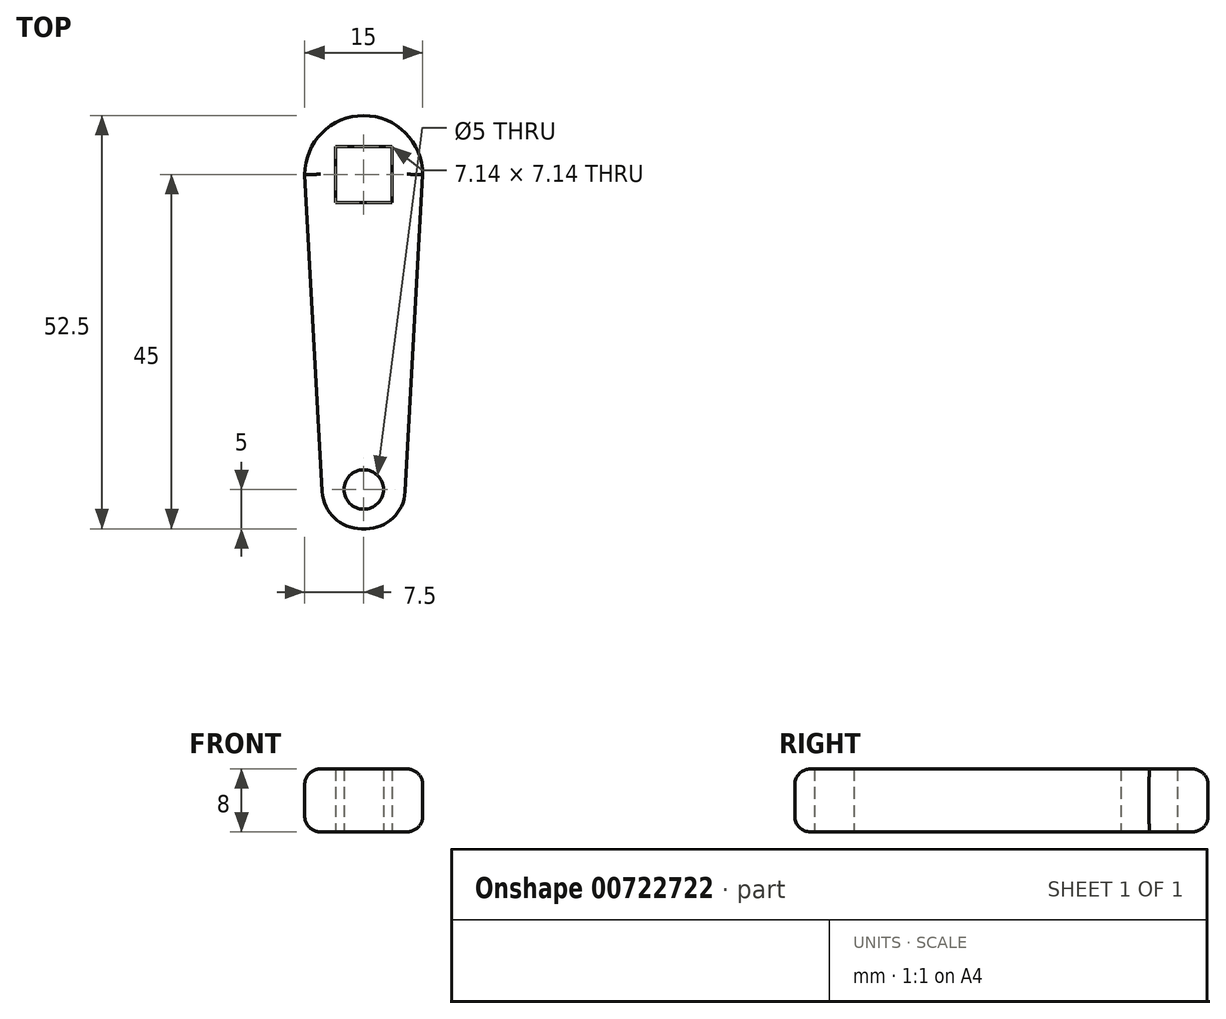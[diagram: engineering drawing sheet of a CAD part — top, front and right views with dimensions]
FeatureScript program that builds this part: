
annotation { "Feature Type Name" : "Feature", "Feature Type Description" : "" }
export const myFeature = defineFeature(function(context is Context, id is Id, definition is map)
    precondition{}
    {
        {
            var Q0;
            Q0=qCreatedBy(makeId("Top.planeOp"),FACE);
            var sketch = newSketch(context, id + "F0", { "sketchPlane" : qUnion([Q0])});
            skCircle(sketch, "E0.cCircle", {"center": v(0, 0) * mm, "radius": 5.05 * mm, "construction": true});
            skArc(sketch, "E1", {"start": v(7.5, 0) * mm, "mid": v(0, 7.5) * mm, "end": v(-7.5, 0) * mm});
            skLineSegment(sketch, "E2", {"start": v(0, 0) * mm, "end": v(0, -45) * mm, "construction": true});
            skLineSegment(sketch, "E3.bottom", {"start": v(-7.5, 0) * mm, "end": v(7.5, 0) * mm});
            skLineSegment(sketch, "E4", {"start": v(0, -45) * mm, "end": v(5, -45) * mm});
            skLineSegment(sketch, "E5", {"start": v(0, -45) * mm, "end": v(-5, -45) * mm});
            skLineSegment(sketch, "E6", {"start": v(-7.5, 0) * mm, "end": v(-5, -45) * mm});
            skLineSegment(sketch, "E7", {"start": v(7.5, 0) * mm, "end": v(5, -45) * mm});
            skLineSegment(sketch, "E8", {"start": v(0, -45) * mm, "end": v(0, -40) * mm, "construction": true});
            skCircle(sketch, "E9", {"center": v(0, -40) * mm, "radius": 2.5 * mm});
            skPoint(sketch, "E10.orphan", {"position": v(2.97, 4.09) * mm});
            skPoint(sketch, "E0.4.end.orphan", {"position": v(0, -5.05) * mm});
            skPoint(sketch, "E11.orphan", {"position": v(-4.8, -1.56) * mm});
            skLineSegment(sketch, "E12.0", {"start": v(3.57, -3.57) * mm, "end": v(-3.57, -3.57) * mm});
            skLineSegment(sketch, "E12.1", {"start": v(-3.57, -3.57) * mm, "end": v(-3.57, 3.57) * mm});
            skLineSegment(sketch, "E12.2", {"start": v(-3.57, 3.57) * mm, "end": v(3.57, 3.57) * mm});
            skLineSegment(sketch, "E12.3", {"start": v(3.57, 3.57) * mm, "end": v(3.57, -3.57) * mm});
            skSolve(sketch);
        }
        {
            var Q0;
            Q0=qSketchRegion(id+"F0",true);
            extrude(context, id + "F1", {"entities" : qUnion([Q0]), "depth" : 8 * mm, "offsetDistance" : 25 * mm});
        }
        {
            var Q0;
            Q0=makeQuery(id+"F1.opExtrude","SWEPT_EDGE",EDGE,{"disambiguationData":[OSD([sQuery(id+"F0.wireOp",EDGE,"E5"),sQuery(id+"F0.wireOp",EDGE,"E6")])]});
            var Q1;
            Q1=makeQuery(id+"F1.opExtrude","SWEPT_EDGE",EDGE,{"disambiguationData":[OSD([sQuery(id+"F0.wireOp",EDGE,"E4"),sQuery(id+"F0.wireOp",EDGE,"E7")])]});
            fillet(context, id + "F2", {"entities" : qUnion([Q0, Q1]), "radius" : 5 * mm, "tangentPropagation" : true, "allowEdgeOverflow" : false});
        }
        {
            var Q0;
            Q0=makeQuery(id+"F1.opExtrude","CAP_EDGE",EDGE,{"disambiguationData":[OSD([sQuery(id+"F0.wireOp",EDGE,"E7")])],"isStart":false});
            var Q1;
            Q1=makeQuery(id+"F1.opExtrude","CAP_EDGE",EDGE,{"disambiguationData":[OSD([sQuery(id+"F0.wireOp",EDGE,"E1")])],"isStart":false});
            var Q2;
            Q2=makeQuery(id+"F1.opExtrude","CAP_EDGE",EDGE,{"disambiguationData":[OSD([sQuery(id+"F0.wireOp",EDGE,"E6")])],"isStart":true});
            var Q3;
            Q3=makeQuery(id+"F1.opExtrude","CAP_EDGE",EDGE,{"disambiguationData":[OSD([sQuery(id+"F0.wireOp",EDGE,"E1")])],"isStart":true});
            fillet(context, id + "F3", {"entities" : qUnion([Q0, Q1, Q2, Q3]), "radius" : 2 * mm, "tangentPropagation" : true, "allowEdgeOverflow" : false});
        }
    });
